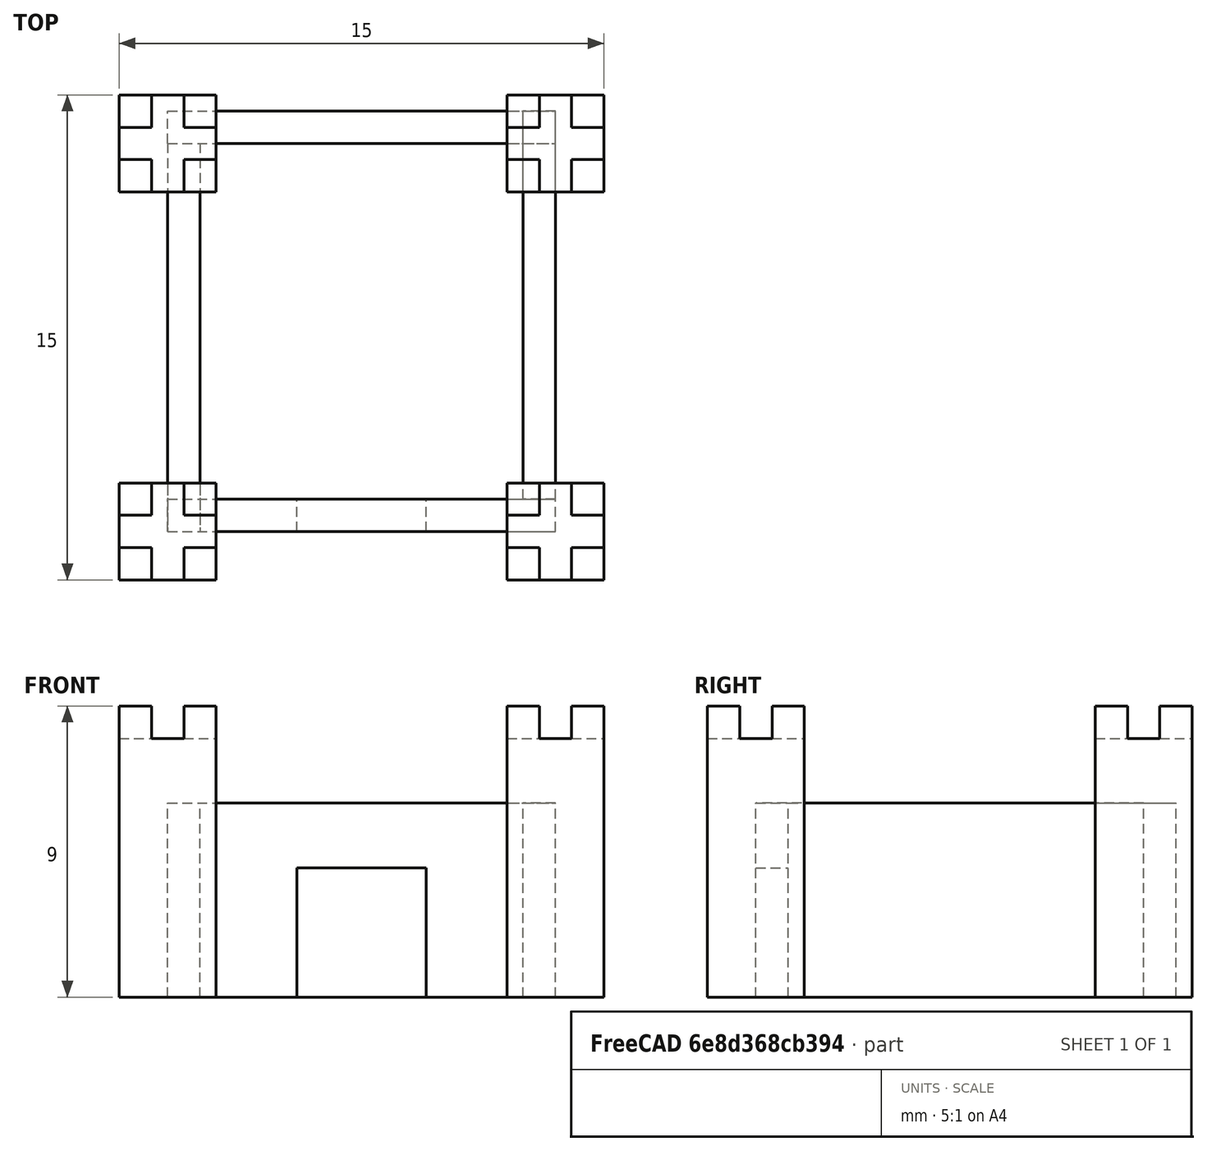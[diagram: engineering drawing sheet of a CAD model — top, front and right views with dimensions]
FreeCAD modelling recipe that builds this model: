
FCSTD DOCUMENT  (FreeCAD 0.19R24291 (Git))
Label: reto5
License: All rights reserved
LicenseURL: http://en.wikipedia.org/wiki/All_rights_reserved
objects: Part::Box×26, Part::MultiFuse×5
note: 31 computed .brp shape members not serialized (recipe doc carries the construction recipe); baked Part::Feature solids carry a one-line shape summary decoded from their .brp

FEATURE [Part::Box] Box  label="Trasera"
  AttacherType = Attacher::AttachEngine3D
  Height = 6
  Length = 12
  Placement = pos=(0,12,0) rot=(0,0,1;0rad)
  Width = 1
FEATURE [Part::Box] Box001  label="Cube001"
  AttacherType = Attacher::AttachEngine3D
  Height = 6
  Length = 4
  Width = 1
FEATURE [Part::Box] Box002  label="Cube002"
  AttacherType = Attacher::AttachEngine3D
  Height = 2
  Length = 4
  Placement = pos=(4,0,4) rot=(0,0,1;0rad)
  Width = 1
FEATURE [Part::Box] Box003  label="Cube003"
  AttacherType = Attacher::AttachEngine3D
  Height = 6
  Length = 4
  Placement = pos=(8,0,0) rot=(0,0,1;0rad)
  Width = 1
FEATURE [Part::MultiFuse] Fusion  label="Frontal"
  Refine = true
  Shapes = -> [Box001,Box002,Box003]
FEATURE [Part::Box] Box004  label="Derecha"
  AttacherType = Attacher::AttachEngine3D
  Height = 6
  Length = 12
  Placement = pos=(12,1,0) rot=(0,0,1;1.5708rad)
  Width = 1
FEATURE [Part::Box] Box005  label="Izquierda"
  AttacherType = Attacher::AttachEngine3D
  Height = 6
  Length = 12
  Placement = pos=(0,12,0) rot=(0,0,1;4.71239rad)
  Width = 1
FEATURE [Part::Box] Box006  label="Cube"
  AttacherType = Attacher::AttachEngine3D
  Height = 8
  Length = 3
  Placement = pos=(-1.5,-1.5,0) rot=(0,0,1;0rad)
  Width = 3
FEATURE [Part::Box] Box007  label="Cube004"
  AttacherType = Attacher::AttachEngine3D
  Height = 1
  Length = 1
  Placement = pos=(0.5,0.5,8) rot=(0,0,1;0rad)
  Width = 1
FEATURE [Part::Box] Box008  label="Cube005"
  AttacherType = Attacher::AttachEngine3D
  Height = 1
  Length = 1
  Placement = pos=(-1.5,0.5,8) rot=(0,0,1;0rad)
  Width = 1
FEATURE [Part::Box] Box009  label="Cube006"
  AttacherType = Attacher::AttachEngine3D
  Height = 1
  Length = 1
  Placement = pos=(0.5,-1.5,8) rot=(0,0,1;0rad)
  Width = 1
FEATURE [Part::Box] Box010  label="Cube007"
  AttacherType = Attacher::AttachEngine3D
  Height = 1
  Length = 1
  Placement = pos=(-1.5,-1.5,8) rot=(0,0,1;0rad)
  Width = 1
FEATURE [Part::MultiFuse] Fusion001  label="Torre di"
  Refine = true
  Shapes = -> [Box006,Box007,Box008,Box009,Box010]
FEATURE [Part::Box] Box011  label="Cube008"
  AttacherType = Attacher::AttachEngine3D
  Height = 1
  Length = 1
  Placement = pos=(0.5,-1.5,8) rot=(0,0,1;0rad)
  Width = 1
FEATURE [Part::Box] Box012  label="Cube009"
  AttacherType = Attacher::AttachEngine3D
  Height = 1
  Length = 1
  Placement = pos=(-1.5,0.5,8) rot=(0,0,1;0rad)
  Width = 1
FEATURE [Part::Box] Box013  label="Cube010"
  AttacherType = Attacher::AttachEngine3D
  Height = 1
  Length = 1
  Placement = pos=(0.5,0.5,8) rot=(0,0,1;0rad)
  Width = 1
FEATURE [Part::Box] Box014  label="Cube011"
  AttacherType = Attacher::AttachEngine3D
  Height = 1
  Length = 1
  Placement = pos=(-1.5,-1.5,8) rot=(0,0,1;0rad)
  Width = 1
FEATURE [Part::Box] Box015  label="Cube012"
  AttacherType = Attacher::AttachEngine3D
  Height = 8
  Length = 3
  Placement = pos=(-1.5,-1.5,0) rot=(0,0,1;0rad)
  Width = 3
FEATURE [Part::MultiFuse] Fusion002  label="Torre dd"
  Placement = pos=(12,0,0) rot=(0,0,1;0rad)
  Refine = true
  Shapes = -> [Box015,Box013,Box012,Box011,Box014]
FEATURE [Part::Box] Box016  label="Cube013"
  AttacherType = Attacher::AttachEngine3D
  Height = 1
  Length = 1
  Placement = pos=(0.5,-1.5,8) rot=(0,0,1;0rad)
  Width = 1
FEATURE [Part::Box] Box017  label="Cube014"
  AttacherType = Attacher::AttachEngine3D
  Height = 1
  Length = 1
  Placement = pos=(-1.5,0.5,8) rot=(0,0,1;0rad)
  Width = 1
FEATURE [Part::Box] Box018  label="Cube015"
  AttacherType = Attacher::AttachEngine3D
  Height = 1
  Length = 1
  Placement = pos=(0.5,0.5,8) rot=(0,0,1;0rad)
  Width = 1
FEATURE [Part::Box] Box019  label="Cube016"
  AttacherType = Attacher::AttachEngine3D
  Height = 1
  Length = 1
  Placement = pos=(-1.5,-1.5,8) rot=(0,0,1;0rad)
  Width = 1
FEATURE [Part::Box] Box020  label="Cube017"
  AttacherType = Attacher::AttachEngine3D
  Height = 8
  Length = 3
  Placement = pos=(-1.5,-1.5,0) rot=(0,0,1;0rad)
  Width = 3
FEATURE [Part::MultiFuse] Fusion003  label="Torre ti"
  Placement = pos=(0,12,0) rot=(0,0,1;0rad)
  Refine = true
  Shapes = -> [Box020,Box018,Box017,Box016,Box019]
FEATURE [Part::Box] Box021  label="Cube018"
  AttacherType = Attacher::AttachEngine3D
  Height = 1
  Length = 1
  Placement = pos=(-1.5,-1.5,8) rot=(0,0,1;0rad)
  Width = 1
FEATURE [Part::Box] Box022  label="Cube019"
  AttacherType = Attacher::AttachEngine3D
  Height = 1
  Length = 1
  Placement = pos=(0.5,0.5,8) rot=(0,0,1;0rad)
  Width = 1
FEATURE [Part::Box] Box023  label="Cube020"
  AttacherType = Attacher::AttachEngine3D
  Height = 8
  Length = 3
  Placement = pos=(-1.5,-1.5,0) rot=(0,0,1;0rad)
  Width = 3
FEATURE [Part::Box] Box024  label="Cube021"
  AttacherType = Attacher::AttachEngine3D
  Height = 1
  Length = 1
  Placement = pos=(0.5,-1.5,8) rot=(0,0,1;0rad)
  Width = 1
FEATURE [Part::Box] Box025  label="Cube022"
  AttacherType = Attacher::AttachEngine3D
  Height = 1
  Length = 1
  Placement = pos=(-1.5,0.5,8) rot=(0,0,1;0rad)
  Width = 1
FEATURE [Part::MultiFuse] Fusion004  label="Torre td"
  Placement = pos=(12,12,0) rot=(0,0,1;0rad)
  Refine = true
  Shapes = -> [Box023,Box022,Box025,Box024,Box021]
